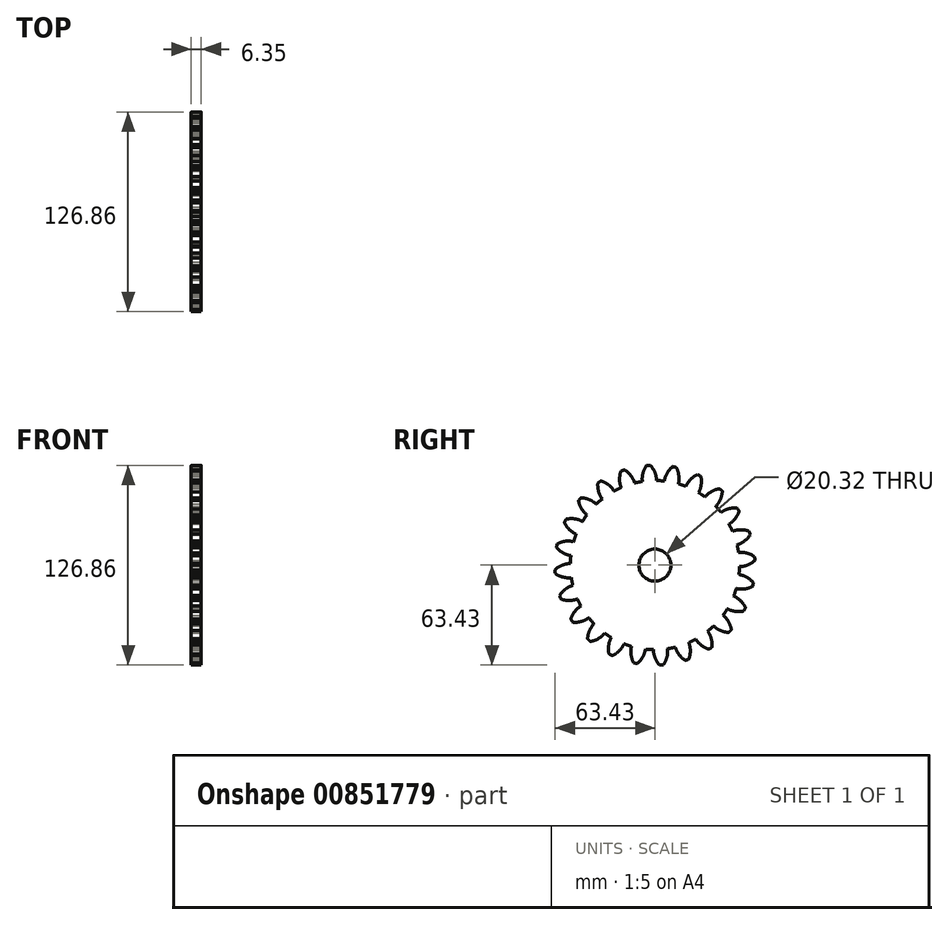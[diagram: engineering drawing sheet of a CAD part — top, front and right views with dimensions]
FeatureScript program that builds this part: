
annotation { "Feature Type Name" : "Feature", "Feature Type Description" : "" }
export const myFeature = defineFeature(function(context is Context, id is Id, definition is map)
    precondition{}
    {
        {
            var Q0;
            Q0=qCreatedBy(makeId("Right.planeOp"),FACE);
            var sketch = newSketch(context, id + "F0", { "sketchPlane" : qUnion([Q0])});
            skCircle(sketch, "E0", {"center": v(0, 0) * mm, "radius": 53.72 * mm});
            skCircle(sketch, "E1", {"center": v(0, 0) * mm, "radius": 58.67 * mm, "construction": true});
            skCircle(sketch, "E2", {"center": v(0, 0) * mm, "radius": 63.5 * mm, "construction": true});
            skLineSegment(sketch, "E3", {"start": v(0, 0) * mm, "end": v(0, 51.74) * mm, "construction": true});
            skLineSegment(sketch, "E4", {"start": v(0, 0) * mm, "end": v(-6.09, 92.87) * mm, "construction": true});
            skLineSegment(sketch, "E5", {"start": v(0, 58.67) * mm, "end": v(-70.37, 58.67) * mm, "construction": true});
            skLineSegment(sketch, "E6", {"start": v(0, 58.67) * mm, "end": v(-73.5, 31.92) * mm, "construction": true});
            skCircle(sketch, "E7", {"center": v(0, 58.67) * mm, "radius": 14.6 * mm, "construction": true});
            skCircle(sketch, "E8", {"center": v(0, 0) * mm, "radius": 55.14 * mm, "construction": true});
            skCircle(sketch, "E9", {"center": v(-13.62, 53.43) * mm, "radius": 14.6 * mm, "construction": true});
            skArc(sketch, "E10", {"start": v(0, 58.67) * mm, "mid": v(-1.24, 61.2) * mm, "end": v(-2.94, 63.43) * mm});
            skArc(sketch, "E11", {"start": v(0.99, 53.71) * mm, "mid": v(0.74, 56.24) * mm, "end": v(0, 58.67) * mm});
            skArc(sketch, "E12.MirrorCS", {"start": v(-7.66, 58.17) * mm, "mid": v(-6.75, 60.83) * mm, "end": v(-5.36, 63.27) * mm});
            skArc(sketch, "E13.MirrorCS", {"start": v(-7.99, 53.12) * mm, "mid": v(-8.07, 55.66) * mm, "end": v(-7.66, 58.17) * mm});
            skArc(sketch, "E14", {"start": v(-2.94, 63.43) * mm, "mid": v(-4.15, 63.39) * mm, "end": v(-5.36, 63.27) * mm});
            skSolve(sketch);
        }
        {
            var Q0;
            {var subQ0=sQuery(id+"F0.wireOp",EDGE,"E0");var subQ1=makeQuery(id+"F0.imprint","INTERSECT",VERTEX,{"derivedFrom":[subQ0,sQuery(id+"F0.wireOp",EDGE,"E11")]});Q0=makeQuery(id+"F0.imprint","IMPRINT",FACE,{"disambiguationData":[TD([[makeQuery(id+"F0.imprint","IMPRINT",EDGE,{"disambiguationData":[TD([[subQ1,-1.0]])],"derivedFrom":subQ0}),1.0]])]});}
            var Q1;
            Q1=makeQuery(id+"F0.imprint","IMPRINT",FACE,{"disambiguationData":[TD([[makeQuery(id+"F0.imprint","IMPRINT",EDGE,{"derivedFrom":sQuery(id+"F0.wireOp",EDGE,"E10")}),1.0]])]});
            extrude(context, id + "F1", {"entities" : qUnion([Q0, Q1]), "oppositeDirection" : true, "depth" : 6.35 * mm, "offsetDistance" : 25.4 * mm});
        }
        {
            var Q0;
            Q0=makeQuery(id+"F1.opExtrude","SWEPT_BODY",BODY,{"disambiguationData":[OSD([sQuery(id+"F0.wireOp",EDGE,"E0"),sQuery(id+"F0.wireOp",EDGE,"E10"),sQuery(id+"F0.wireOp",EDGE,"E11"),sQuery(id+"F0.wireOp",EDGE,"E12.MirrorCS"),sQuery(id+"F0.wireOp",EDGE,"E13.MirrorCS"),sQuery(id+"F0.wireOp",EDGE,"E14")])]});
            var Q1;
            Q1=makeQuery(id+"F1.opExtrude","SWEPT_FACE",FACE,{"disambiguationData":[OSD([sQuery(id+"F0.wireOp",EDGE,"E0")])]});
            circularPattern(context, id + "F2", {"operationType" : NewBodyOperationType.ADD, "entities" : qUnion([Q0]), "axis" : qUnion([Q1]), "angle" : 360 * degree, "instanceCount" : 24, "equalSpace" : true});
        }
        {
            var Q0;
            {var subQ0=makeQuery(id+"F1.opExtrude","CAP_FACE",FACE,{"disambiguationData":[OSD([sQuery(id+"F0.wireOp",EDGE,"E0"),sQuery(id+"F0.wireOp",EDGE,"E10"),sQuery(id+"F0.wireOp",EDGE,"E11"),sQuery(id+"F0.wireOp",EDGE,"E12.MirrorCS"),sQuery(id+"F0.wireOp",EDGE,"E13.MirrorCS"),sQuery(id+"F0.wireOp",EDGE,"E14")])],"isStart":false});Q0=makeQuery(id+"F2.boolean.opBoolean","MERGE",FACE,{"derivedFrom":[subQ0,makeQuery(id+"F2.opPattern","COPY",FACE,{"derivedFrom":subQ0,"instanceName":"1"}),makeQuery(id+"F2.opPattern","COPY",FACE,{"derivedFrom":subQ0,"instanceName":"2"}),makeQuery(id+"F2.opPattern","COPY",FACE,{"derivedFrom":subQ0,"instanceName":"3"}),makeQuery(id+"F2.opPattern","COPY",FACE,{"derivedFrom":subQ0,"instanceName":"4"}),makeQuery(id+"F2.opPattern","COPY",FACE,{"derivedFrom":subQ0,"instanceName":"5"}),makeQuery(id+"F2.opPattern","COPY",FACE,{"derivedFrom":subQ0,"instanceName":"6"}),makeQuery(id+"F2.opPattern","COPY",FACE,{"derivedFrom":subQ0,"instanceName":"7"}),makeQuery(id+"F2.opPattern","COPY",FACE,{"derivedFrom":subQ0,"instanceName":"8"}),makeQuery(id+"F2.opPattern","COPY",FACE,{"derivedFrom":subQ0,"instanceName":"9"}),makeQuery(id+"F2.opPattern","COPY",FACE,{"derivedFrom":subQ0,"instanceName":"10"}),makeQuery(id+"F2.opPattern","COPY",FACE,{"derivedFrom":subQ0,"instanceName":"11"}),makeQuery(id+"F2.opPattern","COPY",FACE,{"derivedFrom":subQ0,"instanceName":"12"}),makeQuery(id+"F2.opPattern","COPY",FACE,{"derivedFrom":subQ0,"instanceName":"13"}),makeQuery(id+"F2.opPattern","COPY",FACE,{"derivedFrom":subQ0,"instanceName":"14"}),makeQuery(id+"F2.opPattern","COPY",FACE,{"derivedFrom":subQ0,"instanceName":"15"}),makeQuery(id+"F2.opPattern","COPY",FACE,{"derivedFrom":subQ0,"instanceName":"16"}),makeQuery(id+"F2.opPattern","COPY",FACE,{"derivedFrom":subQ0,"instanceName":"17"}),makeQuery(id+"F2.opPattern","COPY",FACE,{"derivedFrom":subQ0,"instanceName":"18"}),makeQuery(id+"F2.opPattern","COPY",FACE,{"derivedFrom":subQ0,"instanceName":"19"}),makeQuery(id+"F2.opPattern","COPY",FACE,{"derivedFrom":subQ0,"instanceName":"20"}),makeQuery(id+"F2.opPattern","COPY",FACE,{"derivedFrom":subQ0,"instanceName":"21"}),makeQuery(id+"F2.opPattern","COPY",FACE,{"derivedFrom":subQ0,"instanceName":"22"}),makeQuery(id+"F2.opPattern","COPY",FACE,{"derivedFrom":subQ0,"instanceName":"23"})]});}
            var sketch = newSketch(context, id + "F3", { "sketchPlane" : qUnion([Q0])});
            skCircle(sketch, "E15", {"center": v(0, 0) * mm, "radius": 10.16 * mm});
            skSolve(sketch);
        }
        {
            var Q0;
            Q0 = qSketchRegion(id + "F3", true);
            extrude(context, id + "F4", {"entities" : qUnion([Q0]), "operationType" : NewBodyOperationType.REMOVE, "oppositeDirection" : true, "depth" : 25.4 * mm, "offsetDistance" : 25.4 * mm});
        }
    });
